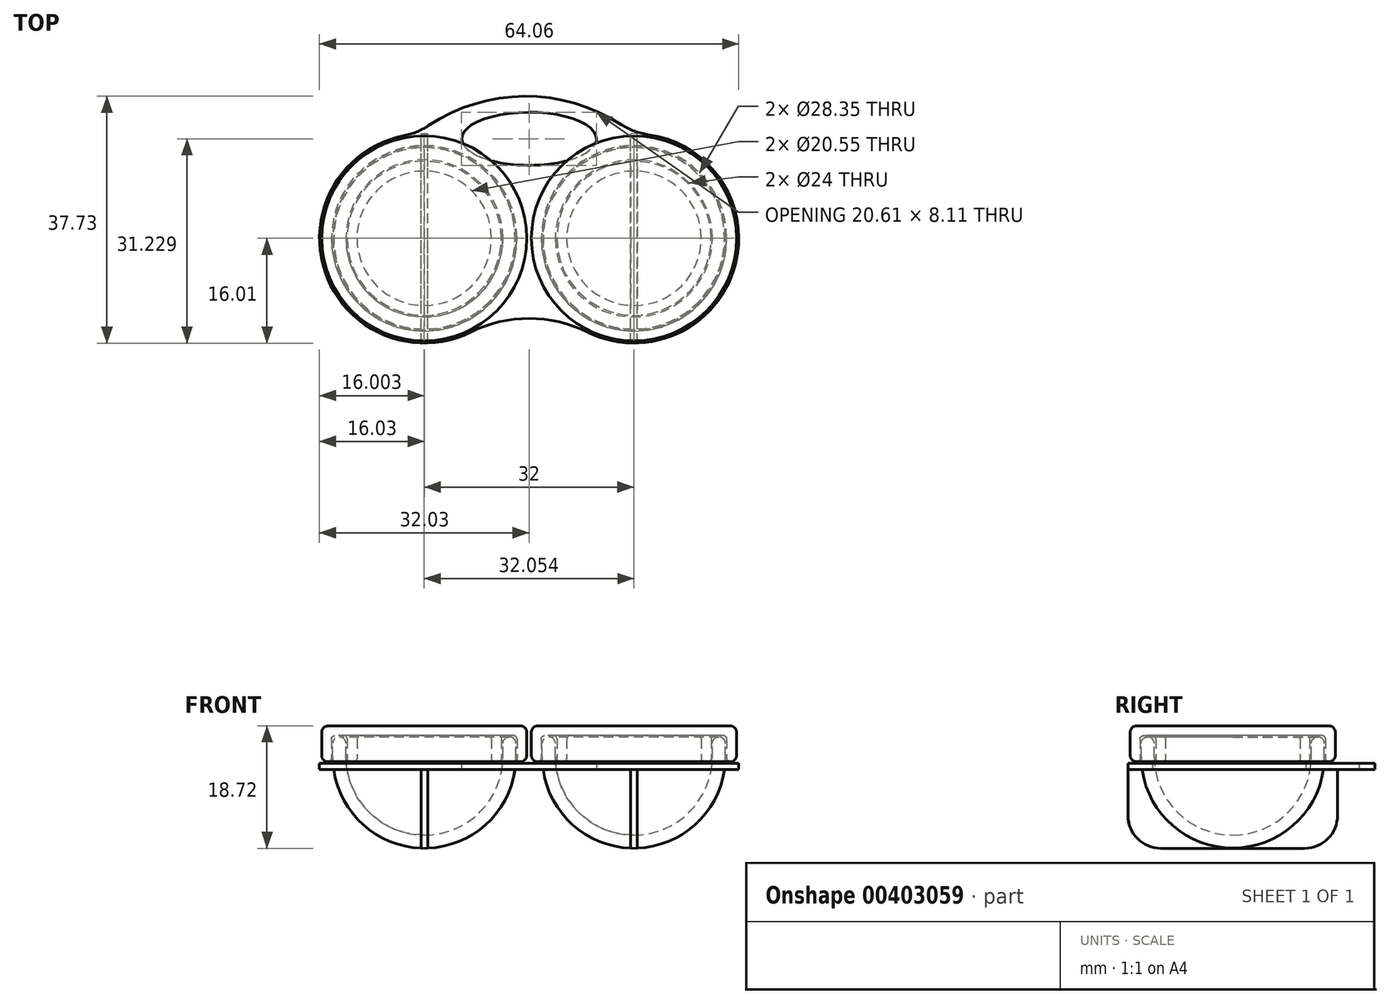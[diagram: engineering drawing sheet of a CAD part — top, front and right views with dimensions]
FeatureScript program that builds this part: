
annotation { "Feature Type Name" : "Feature", "Feature Type Description" : "" }
export const myFeature = defineFeature(function(context is Context, id is Id, definition is map)
    precondition{}
    {
        {
            var Q0;
            Q0=qCreatedBy(makeId("Front.planeOp"),FACE);
            var sketch = newSketch(context, id + "F0", { "sketchPlane" : qUnion([Q0])});
            skArc(sketch, "E0", {"start": v(-28, 14) * mm, "mid": v(-24.49, 5.51) * mm, "end": v(-16, 2) * mm});
            skArc(sketch, "E1", {"start": v(-30, 14) * mm, "mid": v(-25.9, 4.1) * mm, "end": v(-16, 0) * mm});
            skLineSegment(sketch, "E2", {"start": v(-30, 14) * mm, "end": v(-30, 17) * mm});
            skLineSegment(sketch, "E3", {"start": v(-30, 17) * mm, "end": v(-28, 17) * mm});
            skLineSegment(sketch, "E4", {"start": v(-28, 17) * mm, "end": v(-28, 14) * mm});
            skLineSegment(sketch, "E5", {"start": v(-16, 2) * mm, "end": v(-16, 0) * mm});
            skLineSegment(sketch, "E6.MirrorCS", {"start": v(30, 14) * mm, "end": v(30, 17) * mm});
            skLineSegment(sketch, "E7.MirrorCS", {"start": v(28, 17) * mm, "end": v(28, 14) * mm});
            skLineSegment(sketch, "E8.MirrorCS", {"start": v(16, 2) * mm, "end": v(16, 0) * mm});
            skLineSegment(sketch, "E9.MirrorCS", {"start": v(30, 17) * mm, "end": v(28, 17) * mm});
            skArc(sketch, "E10.MirrorCS", {"start": v(30, 14) * mm, "mid": v(25.9, 4.1) * mm, "end": v(16, 0) * mm});
            skArc(sketch, "E11.MirrorCS", {"start": v(28, 14) * mm, "mid": v(24.49, 5.51) * mm, "end": v(16, 2) * mm});
            skSolve(sketch);
        }
        {
            var Q0;
            Q0=makeQuery(id+"F0.imprint","IMPRINT",FACE,{"disambiguationData":[TD([[makeQuery(id+"F0.imprint","IMPRINT",EDGE,{"derivedFrom":sQuery(id+"F0.wireOp",EDGE,"E0")}),-1.0]])]});
            var Q1;
            Q1=sQuery(id+"F0.wireOp",EDGE,"E5");
            revolve(context, id + "F1", {"entities" : qUnion([Q0]), "axis" : qUnion([Q1]), "revolveType" : RevolveType.FULL});
        }
        {
            var Q0;
            Q0=makeQuery(id+"F0.imprint","IMPRINT",FACE,{"disambiguationData":[TD([[makeQuery(id+"F0.imprint","IMPRINT",EDGE,{"derivedFrom":sQuery(id+"F0.wireOp",EDGE,"E6.MirrorCS")}),1.0]])]});
            var Q1;
            Q1=sQuery(id+"F0.wireOp",EDGE,"E8.MirrorCS");
            revolve(context, id + "F2", {"entities" : qUnion([Q0]), "axis" : qUnion([Q1]), "revolveType" : RevolveType.FULL});
        }
        {
            var Q0;
            Q0=qCreatedBy(makeId("Front.planeOp"),FACE);
            var sketch = newSketch(context, id + "F3", { "sketchPlane" : qUnion([Q0])});
            skLineSegment(sketch, "E12", {"start": v(-30.2, 13.2) * mm, "end": v(-30.2, 17.2) * mm});
            skLineSegment(sketch, "E13", {"start": v(-30.2, 17.2) * mm, "end": v(-27.8, 17.2) * mm});
            skLineSegment(sketch, "E14", {"start": v(-27.8, 17.2) * mm, "end": v(-27.8, 13.2) * mm});
            skLineSegment(sketch, "E15", {"start": v(-30.2, 13.2) * mm, "end": v(-31.7, 13.2) * mm});
            skLineSegment(sketch, "E16", {"start": v(-31.7, 13.2) * mm, "end": v(-31.7, 18.7) * mm});
            skLineSegment(sketch, "E17", {"start": v(-16.03, 0) * mm, "end": v(-16.03, 25.41) * mm, "construction": true});
            skLineSegment(sketch, "E18", {"start": v(-31.7, 18.7) * mm, "end": v(-16.03, 18.7) * mm});
            skLineSegment(sketch, "E19", {"start": v(-16.03, 18.7) * mm, "end": v(-16.03, 17.2) * mm});
            skLineSegment(sketch, "E20", {"start": v(-16.03, 17.2) * mm, "end": v(-26.3, 17.2) * mm});
            skLineSegment(sketch, "E21", {"start": v(-26.3, 17.2) * mm, "end": v(-26.3, 13.2) * mm});
            skLineSegment(sketch, "E22", {"start": v(-26.3, 13.2) * mm, "end": v(-27.8, 13.2) * mm});
            skLineSegment(sketch, "E23.MirrorCS", {"start": v(30.2, 17.2) * mm, "end": v(27.8, 17.2) * mm});
            skLineSegment(sketch, "E24.MirrorCS", {"start": v(26.3, 13.2) * mm, "end": v(27.8, 13.2) * mm});
            skLineSegment(sketch, "E25.MirrorCS", {"start": v(30.2, 13.2) * mm, "end": v(31.7, 13.2) * mm});
            skLineSegment(sketch, "E26.MirrorCS", {"start": v(16.03, 18.7) * mm, "end": v(16.03, 17.2) * mm});
            skLineSegment(sketch, "E27.MirrorCS", {"start": v(27.8, 17.2) * mm, "end": v(27.8, 13.2) * mm});
            skLineSegment(sketch, "E28.MirrorCS", {"start": v(26.3, 17.2) * mm, "end": v(26.3, 13.2) * mm});
            skLineSegment(sketch, "E29.MirrorCS", {"start": v(31.7, 13.2) * mm, "end": v(31.7, 18.7) * mm});
            skLineSegment(sketch, "E30.MirrorCS", {"start": v(31.7, 18.7) * mm, "end": v(16.03, 18.7) * mm});
            skLineSegment(sketch, "E31.MirrorCS", {"start": v(30.2, 13.2) * mm, "end": v(30.2, 17.2) * mm});
            skLineSegment(sketch, "E32.MirrorCS", {"start": v(16.03, 17.2) * mm, "end": v(26.3, 17.2) * mm});
            skLineSegment(sketch, "E33.MirrorCS", {"start": v(16.03, 0) * mm, "end": v(16.03, 25.41) * mm, "construction": true});
            skSolve(sketch);
        }
        {
            var Q0;
            Q0=makeQuery(id+"F1.opRevolve","SWEPT_EDGE",EDGE,{"disambiguationData":[OSD([sQuery(id+"F0.wireOp",EDGE,"E2"),sQuery(id+"F0.wireOp",EDGE,"E3")])]});
            var Q1;
            Q1=makeQuery(id+"F1.opRevolve","SWEPT_EDGE",EDGE,{"disambiguationData":[OSD([sQuery(id+"F0.wireOp",EDGE,"E3"),sQuery(id+"F0.wireOp",EDGE,"E4")])]});
            var Q2;
            Q2=makeQuery(id+"F2.opRevolve","SWEPT_EDGE",EDGE,{"disambiguationData":[OSD([sQuery(id+"F0.wireOp",EDGE,"E6.MirrorCS"),sQuery(id+"F0.wireOp",EDGE,"E9.MirrorCS")])]});
            var Q3;
            Q3=makeQuery(id+"F2.opRevolve","SWEPT_EDGE",EDGE,{"disambiguationData":[OSD([sQuery(id+"F0.wireOp",EDGE,"E7.MirrorCS"),sQuery(id+"F0.wireOp",EDGE,"E9.MirrorCS")])]});
            fillet(context, id + "F4", {"entities" : qUnion([Q0, Q1, Q2, Q3]), "radius" : 1 * mm, "tangentPropagation" : true, "allowEdgeOverflow" : false});
        }
        {
            var Q0;
            Q0=makeQuery(id+"F3.imprint","IMPRINT",FACE,{"disambiguationData":[TD([[makeQuery(id+"F3.imprint","IMPRINT",EDGE,{"derivedFrom":sQuery(id+"F3.wireOp",EDGE,"E12")}),1.0]])]});
            var Q1;
            Q1=sQuery(id+"F3.wireOp",EDGE,"E17");
            revolve(context, id + "F5", {"entities" : qUnion([Q0]), "axis" : qUnion([Q1]), "revolveType" : RevolveType.FULL});
        }
        {
            var Q0;
            Q0=makeQuery(id+"F3.imprint","IMPRINT",FACE,{"disambiguationData":[TD([[makeQuery(id+"F3.imprint","IMPRINT",EDGE,{"derivedFrom":sQuery(id+"F3.wireOp",EDGE,"E23.MirrorCS")}),-1.0]])]});
            var Q1;
            Q1=sQuery(id+"F3.wireOp",EDGE,"E33.MirrorCS");
            revolve(context, id + "F6", {"entities" : qUnion([Q0]), "axis" : qUnion([Q1]), "revolveType" : RevolveType.FULL});
        }
        {
            var Q0;
            Q0=makeQuery(id+"F5.opRevolve","SWEPT_EDGE",EDGE,{"disambiguationData":[OSD([sQuery(id+"F3.wireOp",EDGE,"E15"),sQuery(id+"F3.wireOp",EDGE,"E16")])]});
            var Q1;
            Q1=makeQuery(id+"F5.opRevolve","SWEPT_EDGE",EDGE,{"disambiguationData":[OSD([sQuery(id+"F3.wireOp",EDGE,"E16"),sQuery(id+"F3.wireOp",EDGE,"E18")])]});
            var Q2;
            Q2=makeQuery(id+"F6.opRevolve","SWEPT_EDGE",EDGE,{"disambiguationData":[OSD([sQuery(id+"F3.wireOp",EDGE,"E25.MirrorCS"),sQuery(id+"F3.wireOp",EDGE,"E29.MirrorCS")])]});
            var Q3;
            Q3=makeQuery(id+"F6.opRevolve","SWEPT_EDGE",EDGE,{"disambiguationData":[OSD([sQuery(id+"F3.wireOp",EDGE,"E29.MirrorCS"),sQuery(id+"F3.wireOp",EDGE,"E30.MirrorCS")])]});
            fillet(context, id + "F7", {"entities" : qUnion([Q0, Q1, Q2, Q3]), "radius" : 1 * mm, "tangentPropagation" : true, "allowEdgeOverflow" : false});
        }
        {
            var Q0;
            Q0=makeQuery(id+"F5.opRevolve","SWEPT_EDGE",EDGE,{"disambiguationData":[OSD([sQuery(id+"F3.wireOp",EDGE,"E12"),sQuery(id+"F3.wireOp",EDGE,"E15")])]});
            var Q1;
            Q1=makeQuery(id+"F5.opRevolve","SWEPT_EDGE",EDGE,{"disambiguationData":[OSD([sQuery(id+"F3.wireOp",EDGE,"E12"),sQuery(id+"F3.wireOp",EDGE,"E13")])]});
            var Q2;
            Q2=makeQuery(id+"F5.opRevolve","SWEPT_EDGE",EDGE,{"disambiguationData":[OSD([sQuery(id+"F3.wireOp",EDGE,"E13"),sQuery(id+"F3.wireOp",EDGE,"E14")])]});
            var Q3;
            Q3=makeQuery(id+"F5.opRevolve","SWEPT_EDGE",EDGE,{"disambiguationData":[OSD([sQuery(id+"F3.wireOp",EDGE,"E14"),sQuery(id+"F3.wireOp",EDGE,"E22")])]});
            var Q4;
            Q4=makeQuery(id+"F5.opRevolve","SWEPT_EDGE",EDGE,{"disambiguationData":[OSD([sQuery(id+"F3.wireOp",EDGE,"E21"),sQuery(id+"F3.wireOp",EDGE,"E22")])]});
            var Q5;
            Q5=makeQuery(id+"F5.opRevolve","SWEPT_EDGE",EDGE,{"disambiguationData":[OSD([sQuery(id+"F3.wireOp",EDGE,"E20"),sQuery(id+"F3.wireOp",EDGE,"E21")])]});
            var Q6;
            Q6=makeQuery(id+"F6.opRevolve","SWEPT_EDGE",EDGE,{"disambiguationData":[OSD([sQuery(id+"F3.wireOp",EDGE,"E25.MirrorCS"),sQuery(id+"F3.wireOp",EDGE,"E31.MirrorCS")])]});
            var Q7;
            Q7=makeQuery(id+"F6.opRevolve","SWEPT_EDGE",EDGE,{"disambiguationData":[OSD([sQuery(id+"F3.wireOp",EDGE,"E24.MirrorCS"),sQuery(id+"F3.wireOp",EDGE,"E27.MirrorCS")])]});
            var Q8;
            Q8=makeQuery(id+"F6.opRevolve","SWEPT_EDGE",EDGE,{"disambiguationData":[OSD([sQuery(id+"F3.wireOp",EDGE,"E24.MirrorCS"),sQuery(id+"F3.wireOp",EDGE,"E28.MirrorCS")])]});
            var Q9;
            Q9=makeQuery(id+"F6.opRevolve","SWEPT_EDGE",EDGE,{"disambiguationData":[OSD([sQuery(id+"F3.wireOp",EDGE,"E28.MirrorCS"),sQuery(id+"F3.wireOp",EDGE,"E32.MirrorCS")])]});
            var Q10;
            Q10=makeQuery(id+"F6.opRevolve","SWEPT_EDGE",EDGE,{"disambiguationData":[OSD([sQuery(id+"F3.wireOp",EDGE,"E23.MirrorCS"),sQuery(id+"F3.wireOp",EDGE,"E27.MirrorCS")])]});
            var Q11;
            Q11=makeQuery(id+"F6.opRevolve","SWEPT_EDGE",EDGE,{"disambiguationData":[OSD([sQuery(id+"F3.wireOp",EDGE,"E23.MirrorCS"),sQuery(id+"F3.wireOp",EDGE,"E31.MirrorCS")])]});
            fillet(context, id + "F8", {"entities" : qUnion([Q0, Q1, Q2, Q3, Q4, Q5, Q6, Q7, Q8, Q9, Q10, Q11]), "radius" : 0.5 * mm, "tangentPropagation" : true, "allowEdgeOverflow" : false});
        }
        {
            var Q0;
            Q0=qCreatedBy(makeId("Top.planeOp"),FACE);
            cPlane(context, id + "F9", {"entities" : qUnion([Q0]), "cplaneType" : CPlaneType.OFFSET, "offset" : 12 * mm, "width" : 150 * mm, "height" : 150 * mm});
        }
        {
            var Q0;
            Q0=qCreatedBy(id+"F9.planeOp",FACE);
            var sketch = newSketch(context, id + "F10", { "sketchPlane" : qUnion([Q0])});
            skArc(sketch, "E34", {"start": v(-19.07, 15.7) * mm, "mid": v(-28.37, 10.18) * mm, "end": v(-32.03, 0) * mm});
            skArc(sketch, "E35", {"start": v(-32.03, 0) * mm, "mid": v(-24.45, -13.6) * mm, "end": v(-8.9, -14.33) * mm});
            skArc(sketch, "E36", {"start": v(18.2, 15.85) * mm, "mid": v(28.08, 10.52) * mm, "end": v(32.03, 0) * mm});
            skArc(sketch, "E37", {"start": v(32.03, 0) * mm, "mid": v(24.45, -13.6) * mm, "end": v(8.9, -14.33) * mm});
            skArc(sketch, "E38.filletArc", {"start": v(8.9, -14.33) * mm, "mid": v(0, -12.23) * mm, "end": v(-8.9, -14.33) * mm});
            skLineSegment(sketch, "E39", {"start": v(-16.03, 0) * mm, "end": v(-16.03, 21.32) * mm, "construction": true});
            skLineSegment(sketch, "E40.MirrorCS", {"start": v(16.03, 0) * mm, "end": v(16.03, 21.32) * mm, "construction": true});
            skArc(sketch, "E41", {"start": v(14.1, 17.38) * mm, "mid": v(-0.69, 21.72) * mm, "end": v(-15.43, 17.2) * mm});
            skArc(sketch, "E42.filletArc", {"start": v(-19.07, 15.7) * mm, "mid": v(-17.18, 16.28) * mm, "end": v(-15.43, 17.2) * mm});
            skArc(sketch, "E43.filletArc", {"start": v(14.1, 17.38) * mm, "mid": v(16.07, 16.39) * mm, "end": v(18.2, 15.85) * mm});
            skEllipse(sketch, "E44", {"center": v(0, 15.22) * mm, "majorRadius": 10.3 * mm, "minorRadius": 4.05 * mm, "majorAxis": v(1, 0)});
            skLineSegment(sketch, "E45", {"start": v(0, 29) * mm, "end": v(0, 21.71) * mm, "construction": true});
            skPoint(sketch, "E45.endSnap0", {"position": v(0, -12.23) * mm});
            skLineSegment(sketch, "E46", {"start": v(0, 21.71) * mm, "end": v(0, -20.67) * mm, "construction": true});
            skLineSegment(sketch, "E47", {"start": v(39.46, 0) * mm, "end": v(-38.8, 0) * mm, "construction": true});
            skCircle(sketch, "E48", {"center": v(-16.03, 0) * mm, "radius": 13 * mm});
            skCircle(sketch, "E49", {"center": v(16.03, 0) * mm, "radius": 13 * mm});
            skLineSegment(sketch, "E50", {"start": v(16.03, 0) * mm, "end": v(16.03, -16) * mm, "construction": true});
            skLineSegment(sketch, "E51", {"start": v(-16.03, 0) * mm, "end": v(-16.03, -20.47) * mm, "construction": true});
            skLineSegment(sketch, "E52", {"start": v(16.03, -16) * mm, "end": v(16.03, -21.54) * mm, "construction": true});
            skSolve(sketch);
        }
        {
            var Q0;
            Q0=makeQuery(id+"F10.imprint","IMPRINT",FACE,{"disambiguationData":[TD([[makeQuery(id+"F10.imprint","IMPRINT",EDGE,{"derivedFrom":sQuery(id+"F10.wireOp",EDGE,"E34")}),1.0]])]});
            extrude(context, id + "F11", {"entities" : qUnion([Q0]), "operationType" : NewBodyOperationType.ADD, "depth" : 1 * mm});
        }
        {
            var Q0;
            Q0=qCreatedBy(makeId("Right.planeOp"),FACE);
            cPlane(context, id + "F12", {"entities" : qUnion([Q0]), "cplaneType" : CPlaneType.OFFSET, "offset" : 15.5 * mm, "width" : 150 * mm, "height" : 150 * mm});
        }
        {
            var Q0;
            Q0=qCreatedBy(makeId("Right.planeOp"),FACE);
            cPlane(context, id + "F13", {"entities" : qUnion([Q0]), "cplaneType" : CPlaneType.OFFSET, "offset" : 15.5 * mm, "oppositeDirection" : true, "width" : 150 * mm, "height" : 150 * mm});
        }
        {
            var Q0;
            Q0=qCreatedBy(id+"F12.planeOp",FACE);
            var sketch = newSketch(context, id + "F14", { "sketchPlane" : qUnion([Q0])});
            skLineSegment(sketch, "E53", {"start": v(-15.99, 12) * mm, "end": v(-15.99, 5) * mm});
            skLineSegment(sketch, "E54", {"start": v(-10.99, 0) * mm, "end": v(0, 0) * mm});
            skPoint(sketch, "E55.visualSharp", {"position": v(-15.99, 0) * mm});
            skArc(sketch, "E55.filletArc", {"start": v(-15.99, 5) * mm, "mid": v(-14.52, 1.46) * mm, "end": v(-10.99, 0) * mm});
            skLineSegment(sketch, "E56", {"start": v(0, 0) * mm, "end": v(-1.1, 0.27) * mm});
            skLineSegment(sketch, "E57", {"start": v(-1.1, 0.27) * mm, "end": v(-4.35, 1.13) * mm});
            skLineSegment(sketch, "E58", {"start": v(-4.35, 1.13) * mm, "end": v(-9.8, 4.55) * mm});
            skLineSegment(sketch, "E59", {"start": v(-9.8, 4.55) * mm, "end": v(-13.46, 11.64) * mm});
            skLineSegment(sketch, "E60", {"start": v(-13.46, 11.64) * mm, "end": v(-13.46, 12.26) * mm});
            skLineSegment(sketch, "E61", {"start": v(-13.46, 12.26) * mm, "end": v(-15.81, 12.26) * mm});
            skLineSegment(sketch, "E62", {"start": v(-15.81, 12.26) * mm, "end": v(-15.99, 12) * mm});
            skLineSegment(sketch, "E63.MirrorCS", {"start": v(15.81, 12.26) * mm, "end": v(15.99, 12) * mm});
            skLineSegment(sketch, "E64.MirrorCS", {"start": v(13.46, 12.26) * mm, "end": v(15.81, 12.26) * mm});
            skLineSegment(sketch, "E65.MirrorCS", {"start": v(13.46, 11.64) * mm, "end": v(13.46, 12.26) * mm});
            skLineSegment(sketch, "E66.MirrorCS", {"start": v(0, 0) * mm, "end": v(1.1, 0.27) * mm});
            skLineSegment(sketch, "E67.MirrorCS", {"start": v(1.1, 0.27) * mm, "end": v(4.35, 1.13) * mm});
            skLineSegment(sketch, "E68.MirrorCS", {"start": v(4.35, 1.13) * mm, "end": v(9.8, 4.55) * mm});
            skPoint(sketch, "E69.MirrorP", {"position": v(15.99, 0) * mm});
            skLineSegment(sketch, "E70.MirrorCS", {"start": v(9.8, 4.55) * mm, "end": v(13.46, 11.64) * mm});
            skLineSegment(sketch, "E71.MirrorCS", {"start": v(15.99, 12) * mm, "end": v(15.99, 5) * mm});
            skLineSegment(sketch, "E72.MirrorCS", {"start": v(10.99, 0) * mm, "end": v(0, 0) * mm});
            skArc(sketch, "E73.MirrorCS", {"start": v(15.99, 5) * mm, "mid": v(14.52, 1.46) * mm, "end": v(10.99, 0) * mm});
            skSolve(sketch);
        }
        {
            var Q0;
            Q0=makeQuery(id+"F14.imprint","IMPRINT",FACE,{"disambiguationData":[TD([[makeQuery(id+"F14.imprint","IMPRINT",EDGE,{"derivedFrom":sQuery(id+"F14.wireOp",EDGE,"E53")}),1.0]])]});
            var Q1;
            Q1=makeQuery(id+"F14.imprint","IMPRINT",FACE,{"disambiguationData":[TD([[makeQuery(id+"F14.imprint","IMPRINT",EDGE,{"derivedFrom":sQuery(id+"F14.wireOp",EDGE,"E63.MirrorCS")}),-1.0]])]});
            extrude(context, id + "F15", {"entities" : qUnion([Q0, Q1]), "operationType" : NewBodyOperationType.ADD, "depth" : 1 * mm, "hasDraft" : true, "draftAngle" : 1 * degree});
        }
        {
            var Q0;
            Q0=qCreatedBy(id+"F13.planeOp",FACE);
            var sketch = newSketch(context, id + "F16", { "sketchPlane" : qUnion([Q0])});
            skLineSegment(sketch, "E74", {"start": v(-16, 12) * mm, "end": v(-16, 5) * mm});
            skLineSegment(sketch, "E75", {"start": v(-11, 0) * mm, "end": v(0, 0) * mm});
            skPoint(sketch, "E76.visualSharp", {"position": v(-16, 0) * mm});
            skArc(sketch, "E76.filletArc", {"start": v(-16, 5) * mm, "mid": v(-14.53, 1.46) * mm, "end": v(-11, 0) * mm});
            skLineSegment(sketch, "E77", {"start": v(0, 0) * mm, "end": v(-1.11, 0.27) * mm});
            skLineSegment(sketch, "E78", {"start": v(-1.11, 0.27) * mm, "end": v(-4.36, 1.13) * mm});
            skLineSegment(sketch, "E79", {"start": v(-4.36, 1.13) * mm, "end": v(-9.8, 4.55) * mm});
            skLineSegment(sketch, "E80", {"start": v(-9.8, 4.55) * mm, "end": v(-13.47, 11.64) * mm});
            skLineSegment(sketch, "E81", {"start": v(-13.47, 11.64) * mm, "end": v(-13.47, 12.26) * mm});
            skLineSegment(sketch, "E82", {"start": v(-13.47, 12.26) * mm, "end": v(-15.82, 12.26) * mm});
            skLineSegment(sketch, "E83", {"start": v(-15.82, 12.26) * mm, "end": v(-16, 12) * mm});
            skLineSegment(sketch, "E84.MirrorCS", {"start": v(15.8, 12.26) * mm, "end": v(15.98, 12) * mm});
            skLineSegment(sketch, "E85.MirrorCS", {"start": v(13.45, 12.26) * mm, "end": v(15.8, 12.26) * mm});
            skLineSegment(sketch, "E86.MirrorCS", {"start": v(13.45, 11.64) * mm, "end": v(13.45, 12.26) * mm});
            skLineSegment(sketch, "E87.MirrorCS", {"start": v(0, 0) * mm, "end": v(1.1, 0.27) * mm});
            skLineSegment(sketch, "E88.MirrorCS", {"start": v(1.1, 0.27) * mm, "end": v(4.34, 1.13) * mm});
            skLineSegment(sketch, "E89.MirrorCS", {"start": v(4.34, 1.13) * mm, "end": v(9.79, 4.55) * mm});
            skPoint(sketch, "E90.MirrorP", {"position": v(15.98, 0) * mm});
            skLineSegment(sketch, "E91.MirrorCS", {"start": v(9.79, 4.55) * mm, "end": v(13.45, 11.64) * mm});
            skLineSegment(sketch, "E92.MirrorCS", {"start": v(15.98, 12) * mm, "end": v(15.98, 5) * mm});
            skLineSegment(sketch, "E93.MirrorCS", {"start": v(10.98, 0) * mm, "end": v(0, 0) * mm});
            skArc(sketch, "E94.MirrorCS", {"start": v(15.98, 5) * mm, "mid": v(14.51, 1.46) * mm, "end": v(10.98, 0) * mm});
            skSolve(sketch);
        }
        {
            var Q0;
            Q0=makeQuery(id+"F16.imprint","IMPRINT",FACE,{"disambiguationData":[TD([[makeQuery(id+"F16.imprint","IMPRINT",EDGE,{"derivedFrom":sQuery(id+"F16.wireOp",EDGE,"E74")}),1.0]])]});
            var Q1;
            Q1=makeQuery(id+"F16.imprint","IMPRINT",FACE,{"disambiguationData":[TD([[makeQuery(id+"F16.imprint","IMPRINT",EDGE,{"derivedFrom":sQuery(id+"F16.wireOp",EDGE,"E84.MirrorCS")}),-1.0]])]});
            extrude(context, id + "F17", {"entities" : qUnion([Q0, Q1]), "operationType" : NewBodyOperationType.ADD, "oppositeDirection" : true, "depth" : 1 * mm, "hasDraft" : true, "draftAngle" : 1 * degree});
        }
    });
